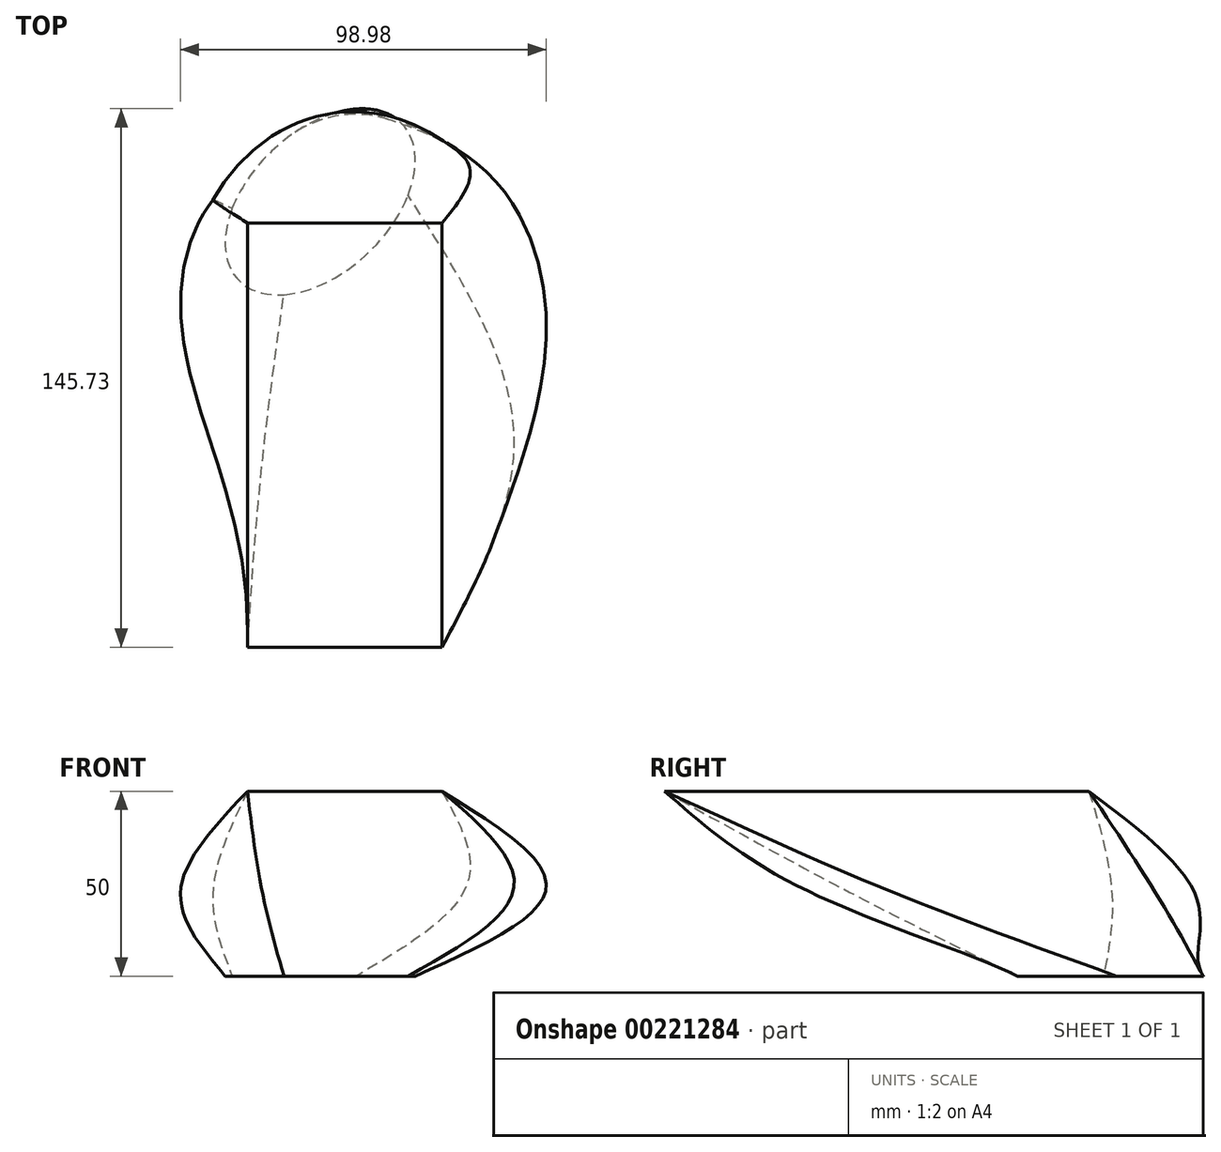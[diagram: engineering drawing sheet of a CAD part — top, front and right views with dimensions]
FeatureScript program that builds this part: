
annotation { "Feature Type Name" : "Feature", "Feature Type Description" : "" }
export const myFeature = defineFeature(function(context is Context, id is Id, definition is map)
    precondition{}
    {
        {
            var Q0;
            Q0=qCreatedBy(makeId("Top.planeOp"),FACE);
            var sketch = newSketch(context, id + "F0", { "sketchPlane" : qUnion([Q0])});
            skEllipse(sketch, "E0", {"center": v(2.74, -4.2) * mm, "majorRadius": 30.6 * mm, "minorRadius": 18.97 * mm, "majorAxis": v(0.72, 0.7)});
            skSolve(sketch);
        }
        {
            var Q0;
            Q0=qCreatedBy(makeId("Top.planeOp"),FACE);
            cPlane(context, id + "F1", {"entities" : qUnion([Q0]), "cplaneType" : CPlaneType.OFFSET, "offset" : 25 * mm, "width" : 150 * mm, "height" : 150 * mm});
        }
        {
            var Q0;
            Q0=qCreatedBy(id+"F1.planeOp",FACE);
            var sketch = newSketch(context, id + "F2", { "sketchPlane" : qUnion([Q0])});
            skEllipse(sketch, "E1", {"center": v(14.58, -36.27) * mm, "majorRadius": 53.92 * mm, "minorRadius": 49.05 * mm, "majorAxis": v(-0.24, 0.97)});
            skSolve(sketch);
        }
        {
            var Q0;
            Q0=qCreatedBy(id+"F1.planeOp",FACE);
            cPlane(context, id + "F3", {"entities" : qUnion([Q0]), "cplaneType" : CPlaneType.OFFSET, "offset" : 25 * mm, "width" : 150 * mm, "height" : 150 * mm});
        }
        {
            var Q0;
            Q0=qCreatedBy(id+"F3.planeOp",FACE);
            var sketch = newSketch(context, id + "F4", { "sketchPlane" : qUnion([Q0])});
            skLineSegment(sketch, "E2.bottom", {"start": v(-16.95, -9.92) * mm, "end": v(35.7, -9.92) * mm});
            skLineSegment(sketch, "E2.top", {"start": v(-16.95, -124.73) * mm, "end": v(35.7, -124.73) * mm});
            skLineSegment(sketch, "E2.left", {"start": v(-16.95, -9.92) * mm, "end": v(-16.95, -124.73) * mm});
            skLineSegment(sketch, "E2.right", {"start": v(35.7, -9.92) * mm, "end": v(35.7, -124.73) * mm});
            skSolve(sketch);
        }
        {
            var Q0;
            Q0=makeQuery(id+"F4.imprint","IMPRINT",FACE,{"disambiguationData":[TD([[makeQuery(id+"F4.imprint","IMPRINT",EDGE,{"derivedFrom":sQuery(id+"F4.wireOp",EDGE,"E2.bottom")}),-1.0]])]});
            var Q1;
            Q1=makeQuery(id+"F2.imprint","IMPRINT",FACE,{"disambiguationData":[TD([[makeQuery(id+"F2.imprint","IMPRINT",EDGE,{"derivedFrom":sQuery(id+"F2.wireOp",EDGE,"E1")}),1.0]])]});
            var Q2;
            Q2=makeQuery(id+"F0.imprint","IMPRINT",FACE,{"disambiguationData":[TD([[makeQuery(id+"F0.imprint","IMPRINT",EDGE,{"derivedFrom":sQuery(id+"F0.wireOp",EDGE,"E0")}),1.0]])]});
            loft(context, id + "F5", {"sheetProfilesArray" : [{ "sheetProfileEntities" : qUnion([Q0]) }, { "sheetProfileEntities" : qUnion([Q1]) }, { "sheetProfileEntities" : qUnion([Q2]) }]});
        }
    });
